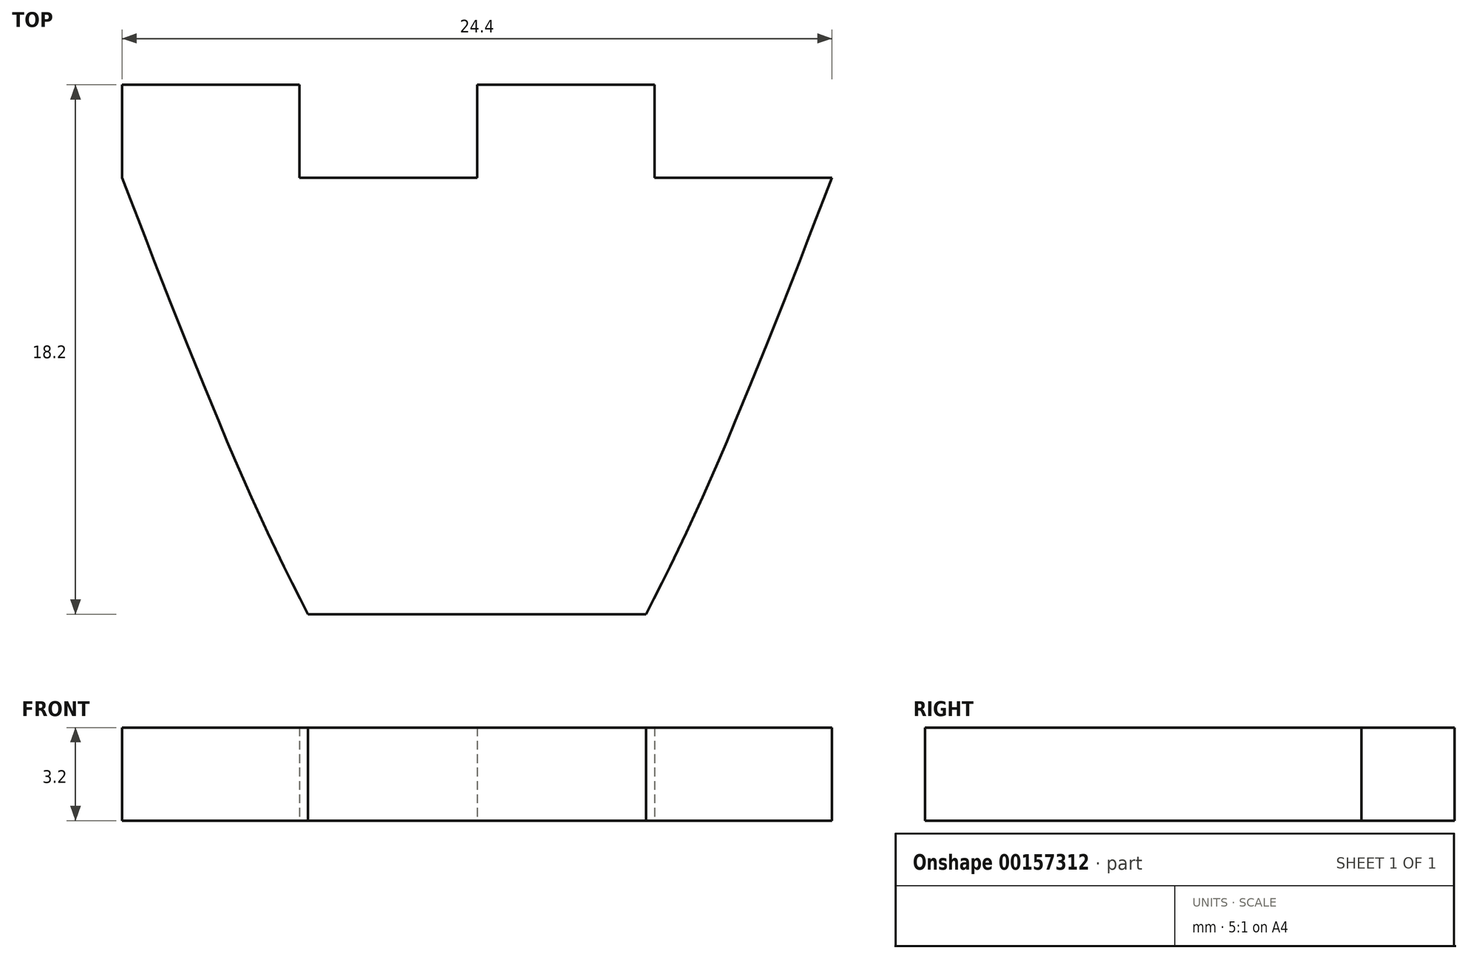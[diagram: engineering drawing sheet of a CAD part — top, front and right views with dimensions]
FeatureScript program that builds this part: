
annotation { "Feature Type Name" : "Feature", "Feature Type Description" : "" }
export const myFeature = defineFeature(function(context is Context, id is Id, definition is map)
    precondition{}
    {
        {
            var Q0;
            Q0=qCreatedBy(makeId("Top.planeOp"),FACE);
            var sketch = newSketch(context, id + "F0", { "sketchPlane" : qUnion([Q0])});
            skLineSegment(sketch, "E0", {"start": v(0, 0) * mm, "end": v(12.2, 0) * mm, "construction": true});
            skLineSegment(sketch, "E1", {"start": v(12.2, 0) * mm, "end": v(-12.2, 0) * mm, "construction": true});
            skLineSegment(sketch, "E2", {"start": v(0, 0) * mm, "end": v(0, -15) * mm, "construction": true});
            skFitSpline(sketch, "E3", {"points": [v(-12.2, 0) * mm, v(0, -21) * mm, v(12.2, 0) * mm], "startDerivative": vector(24.4, -63) * mm, "endDerivative": vector(24.4, 63) * mm});
            skLineSegment(sketch, "E4", {"start": v(-12.2, 0) * mm, "end": v(-12.2, 3.2) * mm});
            skLineSegment(sketch, "E5", {"start": v(-12.2, 3.2) * mm, "end": v(-6.1, 3.2) * mm});
            skLineSegment(sketch, "E6", {"start": v(-6.1, 3.2) * mm, "end": v(-6.1, 0) * mm});
            skLineSegment(sketch, "E7", {"start": v(-6.1, 0) * mm, "end": v(0, 0) * mm});
            skLineSegment(sketch, "E8", {"start": v(0, 0) * mm, "end": v(0, 3.2) * mm});
            skLineSegment(sketch, "E9", {"start": v(0, 3.2) * mm, "end": v(6.1, 3.2) * mm});
            skLineSegment(sketch, "E10", {"start": v(6.1, 3.2) * mm, "end": v(6.1, 0) * mm});
            skLineSegment(sketch, "E11", {"start": v(6.1, 0) * mm, "end": v(12.2, 0) * mm});
            skLineSegment(sketch, "E12", {"start": v(-5.8, -15) * mm, "end": v(5.8, -15) * mm});
            skSolve(sketch);
        }
        {
            var Q0;
            Q0=makeQuery(id+"F0.imprint","IMPRINT",FACE,{"disambiguationData":[TD([[makeQuery(id+"F0.imprint","IMPRINT",EDGE,{"derivedFrom":sQuery(id+"F0.wireOp",EDGE,"E3")}),1.0]])]});
            extrude(context, id + "F1", {"entities" : qUnion([Q0]), "endBound" : BoundingType.SYMMETRIC, "depth" : 3.2 * mm});
        }
    });
